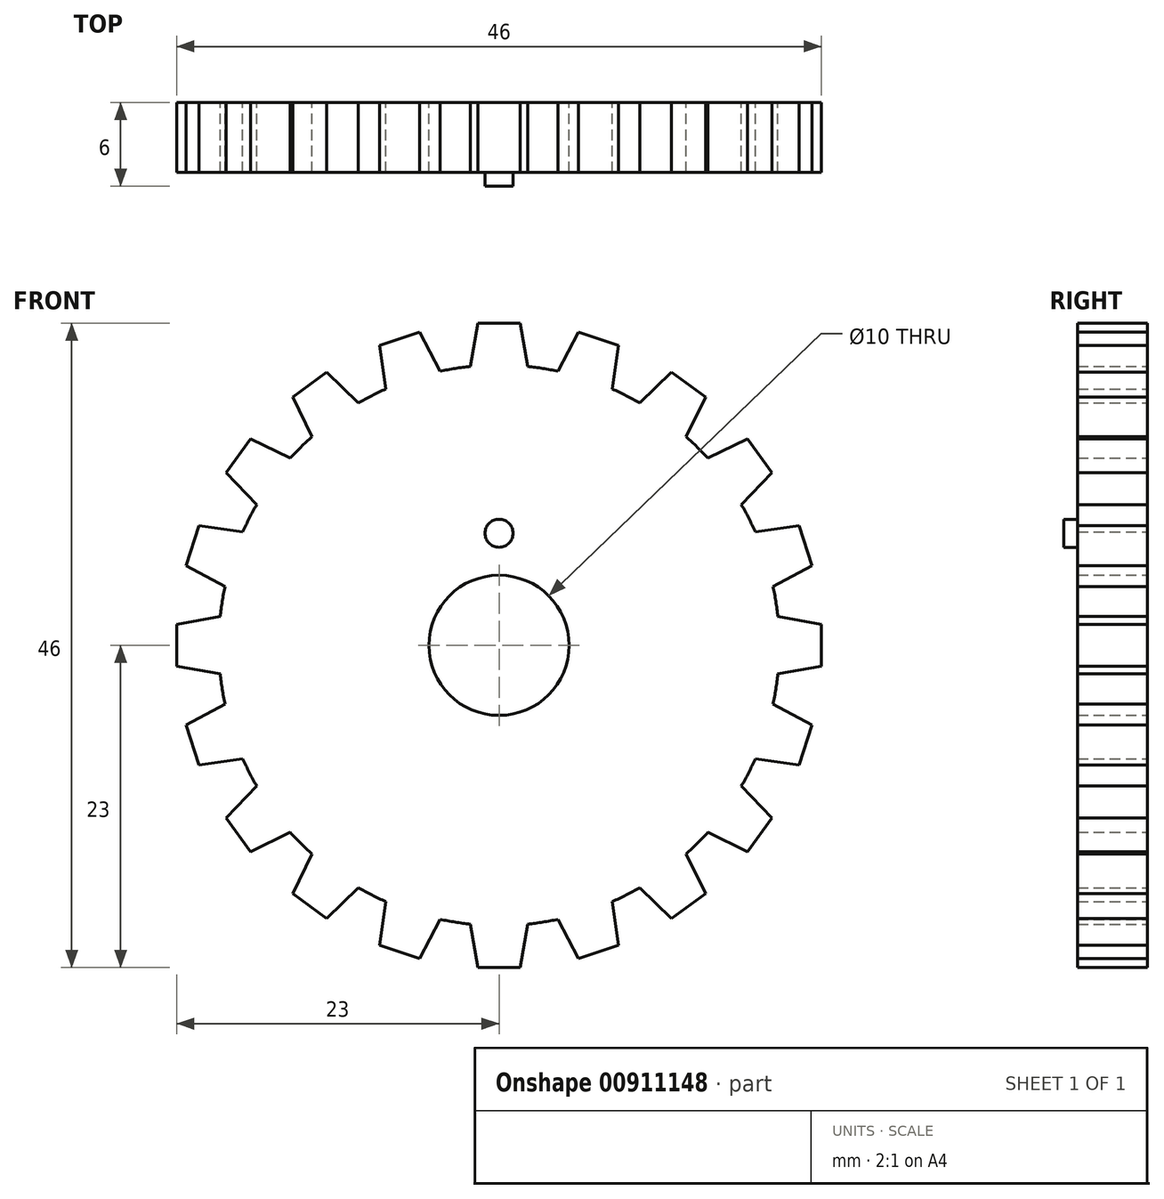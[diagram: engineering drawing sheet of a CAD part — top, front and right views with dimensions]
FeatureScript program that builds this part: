
annotation { "Feature Type Name" : "Feature", "Feature Type Description" : "" }
export const myFeature = defineFeature(function(context is Context, id is Id, definition is map)
    precondition{}
    {
        {
            var Q0;
            Q0=qCreatedBy(makeId("Front.planeOp"),FACE);
            var sketch = newSketch(context, id + "F0", { "sketchPlane" : qUnion([Q0])});
            skCircle(sketch, "E0", {"center": v(0, 0) * mm, "radius": 5 * mm});
            skCircle(sketch, "E1", {"center": v(0, 0) * mm, "radius": 20 * mm});
            skLineSegment(sketch, "E2", {"start": v(2.05, 19.9) * mm, "end": v(1.5, 23) * mm});
            skLineSegment(sketch, "E3", {"start": v(1.5, 23) * mm, "end": v(-1.5, 23) * mm});
            skLineSegment(sketch, "E4.MirrorCS", {"start": v(-2.05, 19.9) * mm, "end": v(-1.5, 23) * mm});
            skLineSegment(sketch, "E5.1.0", {"start": v(-4.2, 19.55) * mm, "end": v(-5.68, 22.34) * mm});
            skLineSegment(sketch, "E5.1.1", {"start": v(-5.68, 22.34) * mm, "end": v(-8.53, 21.41) * mm});
            skLineSegment(sketch, "E5.1.2", {"start": v(-8.1, 18.29) * mm, "end": v(-8.53, 21.41) * mm});
            skLineSegment(sketch, "E5.2.0", {"start": v(-10.04, 17.3) * mm, "end": v(-12.3, 19.49) * mm});
            skLineSegment(sketch, "E5.2.1", {"start": v(-12.3, 19.49) * mm, "end": v(-14.73, 17.73) * mm});
            skLineSegment(sketch, "E5.2.2", {"start": v(-13.35, 14.9) * mm, "end": v(-14.73, 17.73) * mm});
            skLineSegment(sketch, "E6.1.3.0", {"start": v(-14.9, 13.35) * mm, "end": v(-17.73, 14.73) * mm});
            skLineSegment(sketch, "E6.3.3.0", {"start": v(-17.73, 14.73) * mm, "end": v(-19.49, 12.3) * mm});
            skLineSegment(sketch, "E6.6.3.0", {"start": v(-17.3, 10.04) * mm, "end": v(-19.49, 12.3) * mm});
            skLineSegment(sketch, "E6.1.4.0", {"start": v(-18.29, 8.1) * mm, "end": v(-21.41, 8.53) * mm});
            skLineSegment(sketch, "E6.3.4.0", {"start": v(-21.41, 8.53) * mm, "end": v(-22.34, 5.68) * mm});
            skLineSegment(sketch, "E6.6.4.0", {"start": v(-19.55, 4.2) * mm, "end": v(-22.34, 5.68) * mm});
            skLineSegment(sketch, "E6.1.5.0", {"start": v(-19.9, 2.05) * mm, "end": v(-23, 1.5) * mm});
            skLineSegment(sketch, "E6.3.5.0", {"start": v(-23, 1.5) * mm, "end": v(-23, -1.5) * mm});
            skLineSegment(sketch, "E6.6.5.0", {"start": v(-19.9, -2.05) * mm, "end": v(-23, -1.5) * mm});
            skLineSegment(sketch, "E6.1.6.0", {"start": v(-19.55, -4.2) * mm, "end": v(-22.34, -5.68) * mm});
            skLineSegment(sketch, "E6.3.6.0", {"start": v(-22.34, -5.68) * mm, "end": v(-21.41, -8.53) * mm});
            skLineSegment(sketch, "E6.6.6.0", {"start": v(-18.29, -8.1) * mm, "end": v(-21.41, -8.53) * mm});
            skLineSegment(sketch, "E6.1.7.0", {"start": v(-17.3, -10.04) * mm, "end": v(-19.49, -12.3) * mm});
            skLineSegment(sketch, "E6.3.7.0", {"start": v(-19.49, -12.3) * mm, "end": v(-17.73, -14.73) * mm});
            skLineSegment(sketch, "E6.6.7.0", {"start": v(-14.9, -13.35) * mm, "end": v(-17.73, -14.73) * mm});
            skLineSegment(sketch, "E6.1.8.0", {"start": v(-13.35, -14.9) * mm, "end": v(-14.73, -17.73) * mm});
            skLineSegment(sketch, "E6.3.8.0", {"start": v(-14.73, -17.73) * mm, "end": v(-12.3, -19.49) * mm});
            skLineSegment(sketch, "E6.6.8.0", {"start": v(-10.04, -17.3) * mm, "end": v(-12.3, -19.49) * mm});
            skLineSegment(sketch, "E6.1.9.0", {"start": v(-8.1, -18.29) * mm, "end": v(-8.53, -21.41) * mm});
            skLineSegment(sketch, "E6.3.9.0", {"start": v(-8.53, -21.41) * mm, "end": v(-5.68, -22.34) * mm});
            skLineSegment(sketch, "E6.6.9.0", {"start": v(-4.2, -19.55) * mm, "end": v(-5.68, -22.34) * mm});
            skLineSegment(sketch, "E7.1.10.0", {"start": v(-2.05, -19.9) * mm, "end": v(-1.5, -23) * mm});
            skLineSegment(sketch, "E7.3.10.0", {"start": v(-1.5, -23) * mm, "end": v(1.5, -23) * mm});
            skLineSegment(sketch, "E7.6.10.0", {"start": v(2.05, -19.9) * mm, "end": v(1.5, -23) * mm});
            skLineSegment(sketch, "E7.1.11.0", {"start": v(4.2, -19.55) * mm, "end": v(5.68, -22.34) * mm});
            skLineSegment(sketch, "E7.3.11.0", {"start": v(5.68, -22.34) * mm, "end": v(8.53, -21.41) * mm});
            skLineSegment(sketch, "E7.6.11.0", {"start": v(8.1, -18.29) * mm, "end": v(8.53, -21.41) * mm});
            skLineSegment(sketch, "E7.1.12.0", {"start": v(10.04, -17.3) * mm, "end": v(12.3, -19.49) * mm});
            skLineSegment(sketch, "E7.3.12.0", {"start": v(12.3, -19.49) * mm, "end": v(14.73, -17.73) * mm});
            skLineSegment(sketch, "E7.6.12.0", {"start": v(13.35, -14.9) * mm, "end": v(14.73, -17.73) * mm});
            skLineSegment(sketch, "E7.1.13.0", {"start": v(14.9, -13.35) * mm, "end": v(17.73, -14.73) * mm});
            skLineSegment(sketch, "E7.3.13.0", {"start": v(17.73, -14.73) * mm, "end": v(19.49, -12.3) * mm});
            skLineSegment(sketch, "E7.6.13.0", {"start": v(17.3, -10.04) * mm, "end": v(19.49, -12.3) * mm});
            skLineSegment(sketch, "E7.1.14.0", {"start": v(18.29, -8.1) * mm, "end": v(21.41, -8.53) * mm});
            skLineSegment(sketch, "E7.3.14.0", {"start": v(21.41, -8.53) * mm, "end": v(22.34, -5.68) * mm});
            skLineSegment(sketch, "E7.6.14.0", {"start": v(19.55, -4.2) * mm, "end": v(22.34, -5.68) * mm});
            skLineSegment(sketch, "E7.1.15.0", {"start": v(19.9, -2.05) * mm, "end": v(23, -1.5) * mm});
            skLineSegment(sketch, "E7.3.15.0", {"start": v(23, -1.5) * mm, "end": v(23, 1.5) * mm});
            skLineSegment(sketch, "E7.6.15.0", {"start": v(19.9, 2.05) * mm, "end": v(23, 1.5) * mm});
            skLineSegment(sketch, "E7.1.16.0", {"start": v(19.55, 4.2) * mm, "end": v(22.34, 5.68) * mm});
            skLineSegment(sketch, "E7.3.16.0", {"start": v(22.34, 5.68) * mm, "end": v(21.41, 8.53) * mm});
            skLineSegment(sketch, "E7.6.16.0", {"start": v(18.29, 8.1) * mm, "end": v(21.41, 8.53) * mm});
            skLineSegment(sketch, "E7.1.17.0", {"start": v(17.3, 10.04) * mm, "end": v(19.49, 12.3) * mm});
            skLineSegment(sketch, "E7.3.17.0", {"start": v(19.49, 12.3) * mm, "end": v(17.73, 14.73) * mm});
            skLineSegment(sketch, "E7.6.17.0", {"start": v(14.9, 13.35) * mm, "end": v(17.73, 14.73) * mm});
            skLineSegment(sketch, "E7.1.18.0", {"start": v(13.35, 14.9) * mm, "end": v(14.73, 17.73) * mm});
            skLineSegment(sketch, "E7.3.18.0", {"start": v(14.73, 17.73) * mm, "end": v(12.3, 19.49) * mm});
            skLineSegment(sketch, "E7.6.18.0", {"start": v(10.04, 17.3) * mm, "end": v(12.3, 19.49) * mm});
            skLineSegment(sketch, "E7.1.19.0", {"start": v(8.1, 18.29) * mm, "end": v(8.53, 21.41) * mm});
            skLineSegment(sketch, "E7.3.19.0", {"start": v(8.53, 21.41) * mm, "end": v(5.68, 22.34) * mm});
            skLineSegment(sketch, "E7.6.19.0", {"start": v(4.2, 19.55) * mm, "end": v(5.68, 22.34) * mm});
            skSolve(sketch);
        }
        {
            var Q0;
            Q0=qSketchRegion(id+"F0",true);
            extrude(context, id + "F1", {"entities" : qUnion([Q0]), "depth" : 5 * mm, "offsetDistance" : 25 * mm});
        }
        {
            var Q0;
            Q0=makeQuery(id+"F1.opExtrude","CAP_FACE",FACE,{"disambiguationData":[OSD([sQuery(id+"F0.wireOp",EDGE,"E0"),sQuery(id+"F0.wireOp",EDGE,"E1"),sQuery(id+"F0.wireOp",EDGE,"E2"),sQuery(id+"F0.wireOp",EDGE,"E3"),sQuery(id+"F0.wireOp",EDGE,"E4.MirrorCS"),sQuery(id+"F0.wireOp",EDGE,"E5.1.0"),sQuery(id+"F0.wireOp",EDGE,"E5.1.1"),sQuery(id+"F0.wireOp",EDGE,"E5.1.2"),sQuery(id+"F0.wireOp",EDGE,"E5.2.0"),sQuery(id+"F0.wireOp",EDGE,"E5.2.1"),sQuery(id+"F0.wireOp",EDGE,"E5.2.2"),sQuery(id+"F0.wireOp",EDGE,"E6.1.3.0"),sQuery(id+"F0.wireOp",EDGE,"E6.3.3.0"),sQuery(id+"F0.wireOp",EDGE,"E6.6.3.0"),sQuery(id+"F0.wireOp",EDGE,"E6.1.4.0"),sQuery(id+"F0.wireOp",EDGE,"E6.3.4.0"),sQuery(id+"F0.wireOp",EDGE,"E6.6.4.0"),sQuery(id+"F0.wireOp",EDGE,"E6.1.5.0"),sQuery(id+"F0.wireOp",EDGE,"E6.3.5.0"),sQuery(id+"F0.wireOp",EDGE,"E6.6.5.0"),sQuery(id+"F0.wireOp",EDGE,"E6.1.6.0"),sQuery(id+"F0.wireOp",EDGE,"E6.3.6.0"),sQuery(id+"F0.wireOp",EDGE,"E6.6.6.0"),sQuery(id+"F0.wireOp",EDGE,"E6.1.7.0"),sQuery(id+"F0.wireOp",EDGE,"E6.3.7.0"),sQuery(id+"F0.wireOp",EDGE,"E6.6.7.0"),sQuery(id+"F0.wireOp",EDGE,"E6.1.8.0"),sQuery(id+"F0.wireOp",EDGE,"E6.3.8.0"),sQuery(id+"F0.wireOp",EDGE,"E6.6.8.0"),sQuery(id+"F0.wireOp",EDGE,"E6.1.9.0"),sQuery(id+"F0.wireOp",EDGE,"E6.3.9.0"),sQuery(id+"F0.wireOp",EDGE,"E6.6.9.0")])],"isStart":false});
            var sketch = newSketch(context, id + "F2", { "sketchPlane" : qUnion([Q0])});
            skCircle(sketch, "E8", {"center": v(0, 8) * mm, "radius": 1 * mm});
            skSolve(sketch);
        }
        {
            var Q0;
            Q0=qSketchRegion(id+"F2",true);
            extrude(context, id + "F3", {"entities" : qUnion([Q0]), "operationType" : NewBodyOperationType.ADD, "depth" : 1 * mm, "offsetDistance" : 25 * mm});
        }
    });
